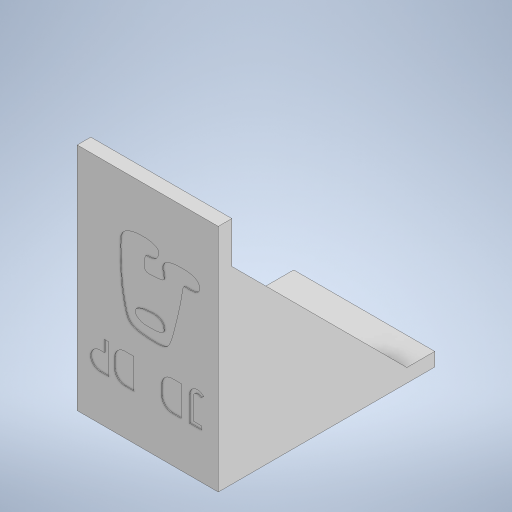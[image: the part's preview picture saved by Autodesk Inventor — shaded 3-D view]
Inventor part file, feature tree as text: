
AUTODESK INVENTOR PART (.ipt)
format: ipt  version: 2023 (Build 270158000, 158)  size: 307,200 bytes
history: native  units: mm
features: extrude x3, sketch x3
ambient origin geometry x8: Origin, YZ Plane, XZ Plane, XY Plane, X Axis, Y Axis, Z Axis, Center Point
bodies: Solid1 (feature_tree)
feature tree (6):
  extrude  "Extrusion1"  Depth=18.0mm
  extrude  "Extrusion2"  Depth=18.0mm
  extrude  "Extrusion3"  Depth=1.0mm
  sketch  "Sketch1"  dims[d0=18.0mm d1=287.0mm]
  sketch  "Sketch2"  dims[d2=287.0mm d3=18.0mm]
  sketch  "Sketch3"  dims[d4=187.0mm d5=0.0mm d6=232.0mm d7=232.0mm d8=18.0mm d9=0.0mm d91=1.0mm d92=0.0mm]
